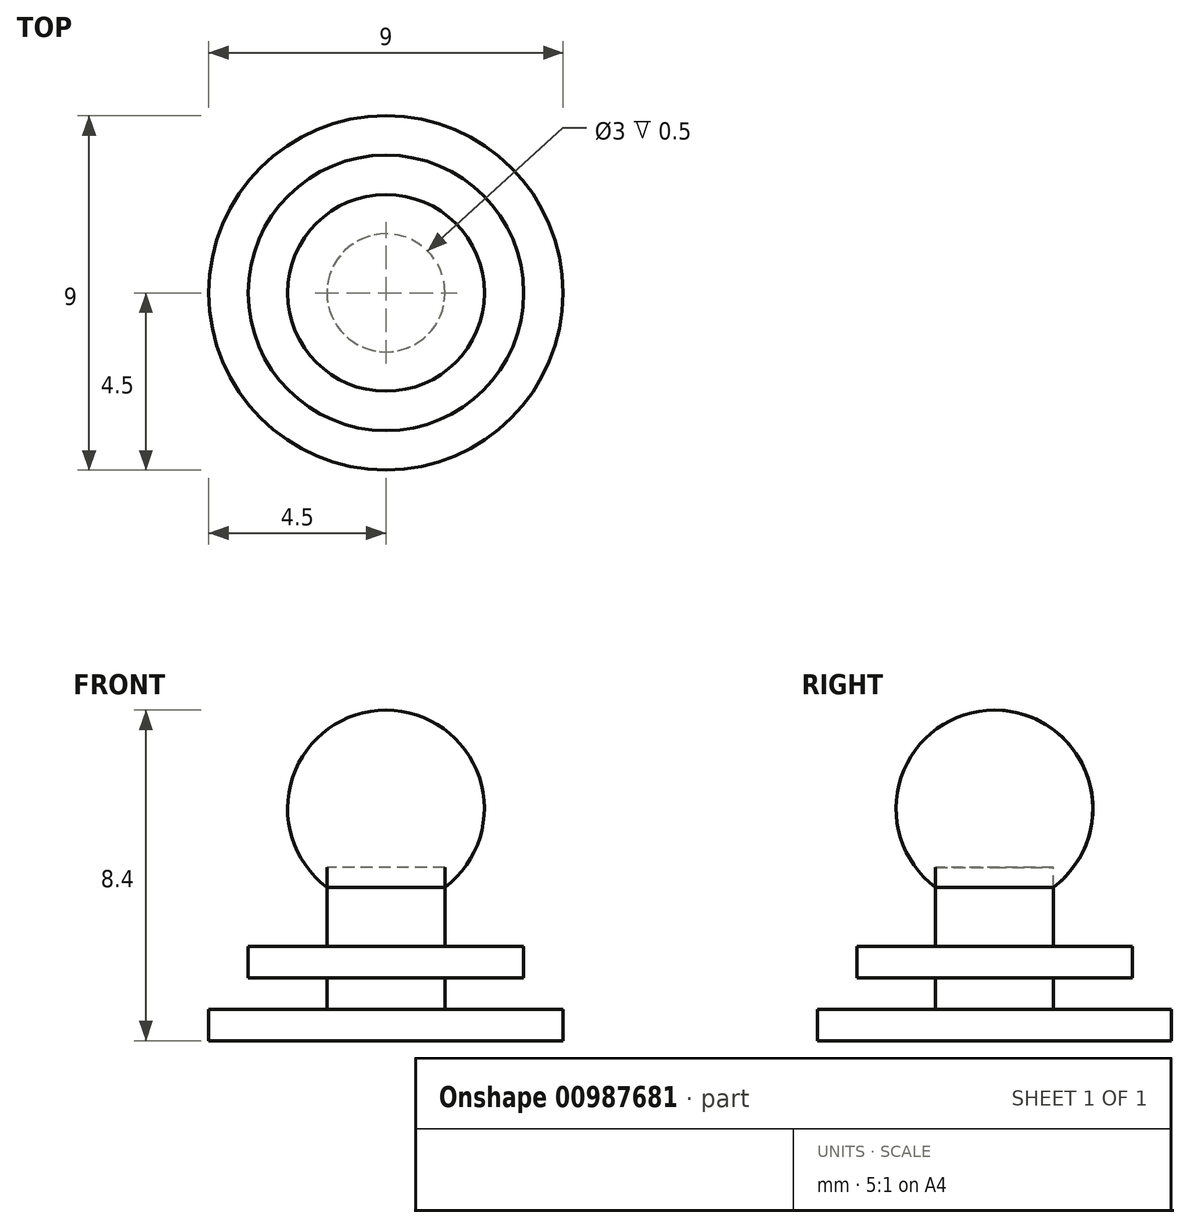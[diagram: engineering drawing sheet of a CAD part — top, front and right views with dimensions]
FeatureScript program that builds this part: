
annotation { "Feature Type Name" : "Feature", "Feature Type Description" : "" }
export const myFeature = defineFeature(function(context is Context, id is Id, definition is map)
    precondition{}
    {
        {
            var Q0;
            Q0=qCreatedBy(makeId("Top.planeOp"),FACE);
            var sketch = newSketch(context, id + "F0", { "sketchPlane" : qUnion([Q0])});
            skCircle(sketch, "E0", {"center": v(0, 0) * mm, "radius": 4.5 * mm});
            skSolve(sketch);
        }
        {
            var Q0;
            Q0=makeQuery(id+"F0.imprint","IMPRINT",FACE,{"disambiguationData":[TD([[makeQuery(id+"F0.imprint","IMPRINT",EDGE,{"derivedFrom":sQuery(id+"F0.wireOp",EDGE,"E0")}),1.0]])]});
            extrude(context, id + "F1", {"entities" : qUnion([Q0]), "depth" : 0.8 * mm, "offsetDistance" : 25 * mm});
        }
        {
            var Q0;
            Q0=makeQuery(id+"F1.opExtrude","CAP_FACE",FACE,{"disambiguationData":[OSD([sQuery(id+"F0.wireOp",EDGE,"E0")])],"isStart":false});
            var sketch = newSketch(context, id + "F2", { "sketchPlane" : qUnion([Q0])});
            skCircle(sketch, "E1", {"center": v(0, 0) * mm, "radius": 1.5 * mm});
            skSolve(sketch);
        }
        {
            var Q0;
            Q0=makeQuery(id+"F2.imprint","IMPRINT",FACE,{"disambiguationData":[TD([[makeQuery(id+"F2.imprint","IMPRINT",EDGE,{"derivedFrom":sQuery(id+"F2.wireOp",EDGE,"E1")}),1.0]])]});
            extrude(context, id + "F3", {"entities" : qUnion([Q0]), "operationType" : NewBodyOperationType.ADD, "depth" : 0.8 * mm, "offsetDistance" : 25 * mm});
        }
        {
            var Q0;
            Q0=makeQuery(id+"F3.opExtrude","CAP_FACE",FACE,{"disambiguationData":[OSD([sQuery(id+"F2.wireOp",EDGE,"E1")])],"isStart":false});
            var sketch = newSketch(context, id + "F4", { "sketchPlane" : qUnion([Q0])});
            skCircle(sketch, "E2", {"center": v(0, 0) * mm, "radius": 3.5 * mm});
            skSolve(sketch);
        }
        {
            var Q0;
            Q0=makeQuery(id+"F4.imprint","IMPRINT",FACE,{"disambiguationData":[TD([[makeQuery(id+"F4.imprint","IMPRINT",EDGE,{"derivedFrom":sQuery(id+"F4.wireOp",EDGE,"E2")}),1.0]])]});
            var Q1;
            Q1=makeQuery(id+"F4.imprint","IMPRINT",FACE,{"disambiguationData":[TD([[makeQuery(id+"F4.imprint","IMPRINT",EDGE,{"derivedFrom":makeQuery(id+"F3.opExtrude","CAP_EDGE",EDGE,{"disambiguationData":[OSD([sQuery(id+"F2.wireOp",EDGE,"E1")])],"isStart":false})}),1.0]])]});
            extrude(context, id + "F5", {"entities" : qUnion([Q0, Q1]), "operationType" : NewBodyOperationType.ADD, "depth" : 0.8 * mm, "offsetDistance" : 25 * mm});
        }
        {
            var Q0;
            Q0=makeQuery(id+"F5.opExtrude","CAP_FACE",FACE,{"disambiguationData":[OSD([sQuery(id+"F4.wireOp",EDGE,"E2")])],"isStart":false});
            var sketch = newSketch(context, id + "F6", { "sketchPlane" : qUnion([Q0])});
            skCircle(sketch, "E3", {"center": v(0, 0) * mm, "radius": 1.5 * mm});
            skSolve(sketch);
        }
        {
            var Q0;
            Q0=makeQuery(id+"F6.imprint","IMPRINT",FACE,{"disambiguationData":[TD([[makeQuery(id+"F6.imprint","IMPRINT",EDGE,{"derivedFrom":sQuery(id+"F6.wireOp",EDGE,"E3")}),1.0]])]});
            extrude(context, id + "F7", {"entities" : qUnion([Q0]), "operationType" : NewBodyOperationType.ADD, "depth" : 2 * mm, "offsetDistance" : 25 * mm});
        }
        {
            var Q0;
            Q0=qCreatedBy(makeId("Right.planeOp"),FACE);
            var sketch = newSketch(context, id + "F8", { "sketchPlane" : qUnion([Q0])});
            skArc(sketch, "E4", {"start": v(1.5, 3.9) * mm, "mid": v(2.37, 6.7) * mm, "end": v(0, 8.4) * mm});
            skLineSegment(sketch, "E5", {"start": v(0, 4.4) * mm, "end": v(1.5, 4.4) * mm});
            skLineSegment(sketch, "E6", {"start": v(1.5, 4.4) * mm, "end": v(1.5, 3.9) * mm});
            skLineSegment(sketch, "E7", {"start": v(0, 4.4) * mm, "end": v(0, 8.4) * mm});
            skLineSegment(sketch, "E8", {"start": v(0, 8.4) * mm, "end": v(0, 4.4) * mm});
            skSolve(sketch);
        }
        {
            var Q0;
            Q0=makeQuery(id+"F8.imprint","IMPRINT",FACE,{"disambiguationData":[TD([[makeQuery(id+"F8.imprint","IMPRINT",EDGE,{"derivedFrom":sQuery(id+"F8.wireOp",EDGE,"E4")}),1.0]])]});
            var Q1;
            Q1=sQuery(id+"F8.wireOp",EDGE,"E8");
            revolve(context, id + "F9", {"surfaceOperationType" : NewSurfaceOperationType.NEW, "entities" : qUnion([Q0]), "axis" : qUnion([Q1]), "revolveType" : RevolveType.FULL});
        }
    });
